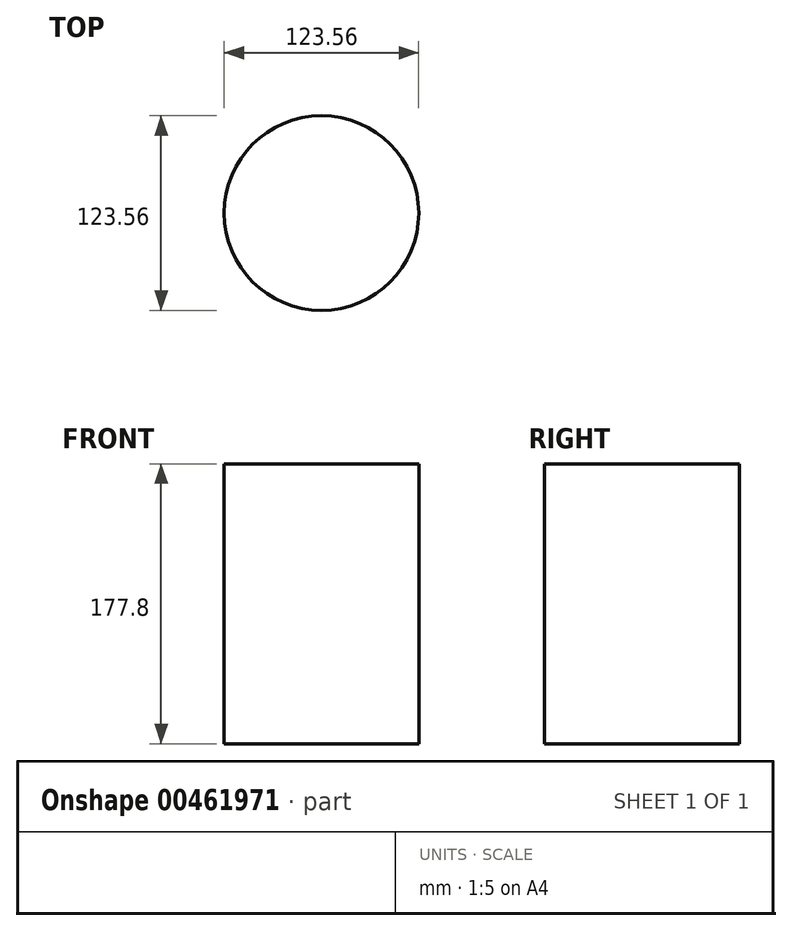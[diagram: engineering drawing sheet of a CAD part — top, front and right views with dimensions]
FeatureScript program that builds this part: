
annotation { "Feature Type Name" : "Feature", "Feature Type Description" : "" }
export const myFeature = defineFeature(function(context is Context, id is Id, definition is map)
    precondition{}
    {
        {
            var Q0;
            Q0=qCreatedBy(makeId("Top.planeOp"),FACE);
            var sketch = newSketch(context, id + "F0", { "sketchPlane" : qUnion([Q0])});
            skCircle(sketch, "E0", {"center": v(0, 0) * mm, "radius": 61.78 * mm});
            skSolve(sketch);
        }
        {
            var Q0;
            Q0=makeQuery(id+"F0.imprint","IMPRINT",FACE,{"disambiguationData":[TD([[makeQuery(id+"F0.imprint","IMPRINT",EDGE,{"derivedFrom":sQuery(id+"F0.wireOp",EDGE,"E0")}),1.0]])]});
            extrude(context, id + "F1", {"entities" : qUnion([Q0]), "depth" : 177.8 * mm, "offsetDistance" : 25.4 * mm});
        }
    });
